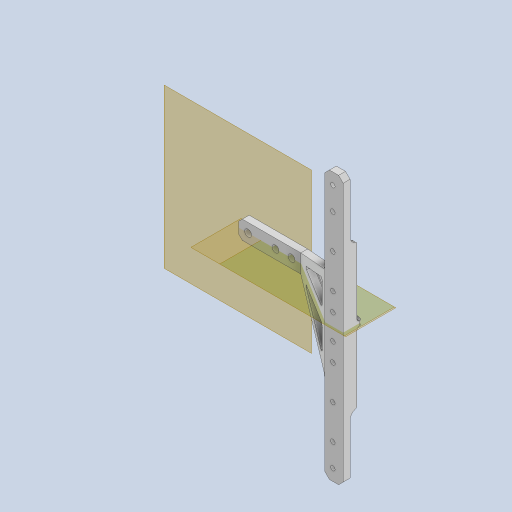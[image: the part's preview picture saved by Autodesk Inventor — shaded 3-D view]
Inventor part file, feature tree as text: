
AUTODESK INVENTOR PART (.ipt)
format: ipt  version: 2023 (Build 270158000, 158)  size: 457,216 bytes
history: native  units: mm
features: sketch x13, extrude x12, other x12, projected_geometry x11, fillet x10, reference x8, thicken_offset x5, plane x4, chamfer x4, loft x1, mirror x1
ambient origin geometry x8: Origin, YZ Plane, XZ Plane, XY Plane, X Axis, Y Axis, Z Axis, Center Point
bodies: Solid1 (feature_tree)
feature tree (81):
  extrude  "Extrusion1"  Depth=87.0mm
  plane  "Work Plane1"
  plane  "Work Plane2"
  extrude  "Extrusion2"  Depth=2.0mm
  sketch  "Sketch3"  dims[d4=2.0mm d5=2.0mm]
  loft  "Loft1"
  plane  "Work Plane3"
  extrude  "Extrusion3"  Depth=3.0mm
  fillet  "Fillet1"  Radius=15.0mm
  extrude  "Extrusion4"  Depth=2.0mm
  fillet  "Fillet2"  Radius=3.0mm
  fillet  "Fillet3"  Radius=3.0mm
  chamfer  "Chamfer1"  Angle=90.0deg  [1 undecoded]
  chamfer  "Chamfer2"  Angle=90.0deg  [1 undecoded]
  extrude  "Extrusion5"  Depth=2.0mm TaperAngle=0.0deg
  fillet  "Fillet4"  Radius=3.0mm
  thicken_offset  "Thicken1"
  thicken_offset  "Thicken2"
  extrude  "Extrusion6"  Depth=2.0mm
  chamfer  "Chamfer3"  Distance=2.0mm
  extrude  "Extrusion7"  Depth=3.0mm TaperAngle=0.0deg
  extrude  "Extrusion8"  Depth=1.0mm
  extrude  "Extrusion9"  Depth=1.0mm
  plane  "Work Plane4"
  mirror  "Mirror1"
  thicken_offset  "Thicken3"
  thicken_offset  "Thicken4"
  thicken_offset  "Thicken5"
  chamfer  "Chamfer5"  Distance=1.5mm
  extrude  "Extrusion10"  Depth=3.0mm
  extrude  "Extrusion11"  Depth=2.0mm TaperAngle=45.0deg
  fillet  "Fillet5"  Radius=2.0mm
  fillet  "Fillet6"  Radius=15.0mm
  extrude  "Extrusion13"  Depth=1.0mm
  fillet  "Fillet7"  Radius=15.0mm
  fillet  "Fillet8"  Radius=8.0mm
  fillet  "Fillet9"  Radius=2.0mm
  fillet  "Fillet10"  Radius=2.0mm
  sketch  "Sketch1"  dims[d0=7.0mm d1=87.0mm]
  reference  "Reference1"
  reference  "Reference2"
  sketch  "Sketch2"  dims[d2=2.0mm d3=2.0mm]
  reference  "Reference3"
  projected_geometry  "Projected Loop1"
  other  "Edges1"
  sketch  "Sketch5"  dims[d6=3.0mm d7=0.0mm d8=8.0mm d9=15.0mm]
  projected_geometry  "Projected Loop3"
  projected_geometry  "Projected Loop4"
  sketch  "Sketch6"  dims[d10=2.0mm d11=2.0mm d12=3.0mm d13=0.0mm d14=3.0mm]
  projected_geometry  "Projected Loop5"
  projected_geometry  "Projected Loop6"
  sketch  "Sketch7"  dims[d15=20.0mm]
  projected_geometry  "Projected Loop7"
  projected_geometry  "Projected Loop8"
  sketch  "Sketch8"  dims[d16=3.0mm]
  projected_geometry  "Projected Loop9"
  reference  "Reference4"
  sketch  "Sketch9"  dims[d17=20.0mm d18=0.0mm d19=90.0deg d20=0.0mm d21=90.0deg]
  reference  "Reference5"
  reference  "Reference6"
  sketch  "Sketch10"  dims[d22=5.0mm d23=2.0mm d24=0.0mm d25=3.0mm]
  reference  "Reference7"
  reference  "Reference8"
  sketch  "Sketch11"  dims[d26=2.0mm d27=2.0mm]
  sketch  "Sketch12"  dims[d28=4.0mm]
  projected_geometry  "Projected Loop10"
  sketch  "Sketch13"  dims[d29=4.0mm]
  projected_geometry  "Projected Loop11"
  sketch  "Sketch15"  dims[d30=2.0mm d31=2.0mm d32=3.0mm d33=0.0mm d34=0.5mm d35=1.0mm d36=1.5mm d37=3.0mm d38=2.0mm d39=2.0mm d40=45.0deg d41=2.0mm d42=2.0mm d43=45.0deg d44=15.0mm d45=8.0mm d46=15.0mm d47=8.0mm d48=2.0mm d49=2.0mm d50=2.0mm d51=2.0mm d52=3.0mm d53=0.0mm d54=1.0mm d55=0.5mm d56=0.5mm d57=0.5mm d58=0.5mm d59=14.0mm d60=8.0mm d61=3.0mm d62=0.0mm d63=1.5mm d64=2.0mm d65=45.0deg d66=7.0mm d67=16.0mm d68=3.0mm d69=0.0mm d70=2.0mm d71=2.0mm d72=3.0mm d73=0.0mm d74=3.0mm d75=0.0mm d79=1.0mm d80=1.0mm d81=1.0mm d82=1.0mm d83=1.0mm d84=1.0mm d85=2.0mm d86=2.0mm d87=45.0deg d88=2.0mm d89=0.0mm d90=25.0mm d91=25.0mm d92=3.0mm d93=63.0mm d94=1.5mm d95=0.0mm d98=3.0mm d99=1.0mm d100=2.0mm d101=2.0mm d102=0.0mm d103=1.0mm d104=1.0mm d105=12.0mm d106=1.0mm]
  projected_geometry  "Projected Loop13"
  parser-record x2  (decoder bookkeeping rows leaked as tree rows — omitted from the tree; the rows remain in map.json)
  other  "body_8d_1.iam"
  other  "leg_2d_1:2"
  other  "leg_holder_2:1"
  other  "leg_1_2d_MIR:2"
  other  "leg_holder_2_MIR:1"
  other  "body_linker_1_8d:1"
  other  "body_8d_wid_1.iam"
  other  "body_linker_1_wid_8d:1"
  other  "leg_2d_1:1"
note: 2 required parameter values undecoded (feature->parameter linkage not recoverable at this tier; creation-order binding heuristic only, values carry confidence <= 0.55)
note: 2 file-system paths scrubbed to <path> (originals preserved in map.json)
